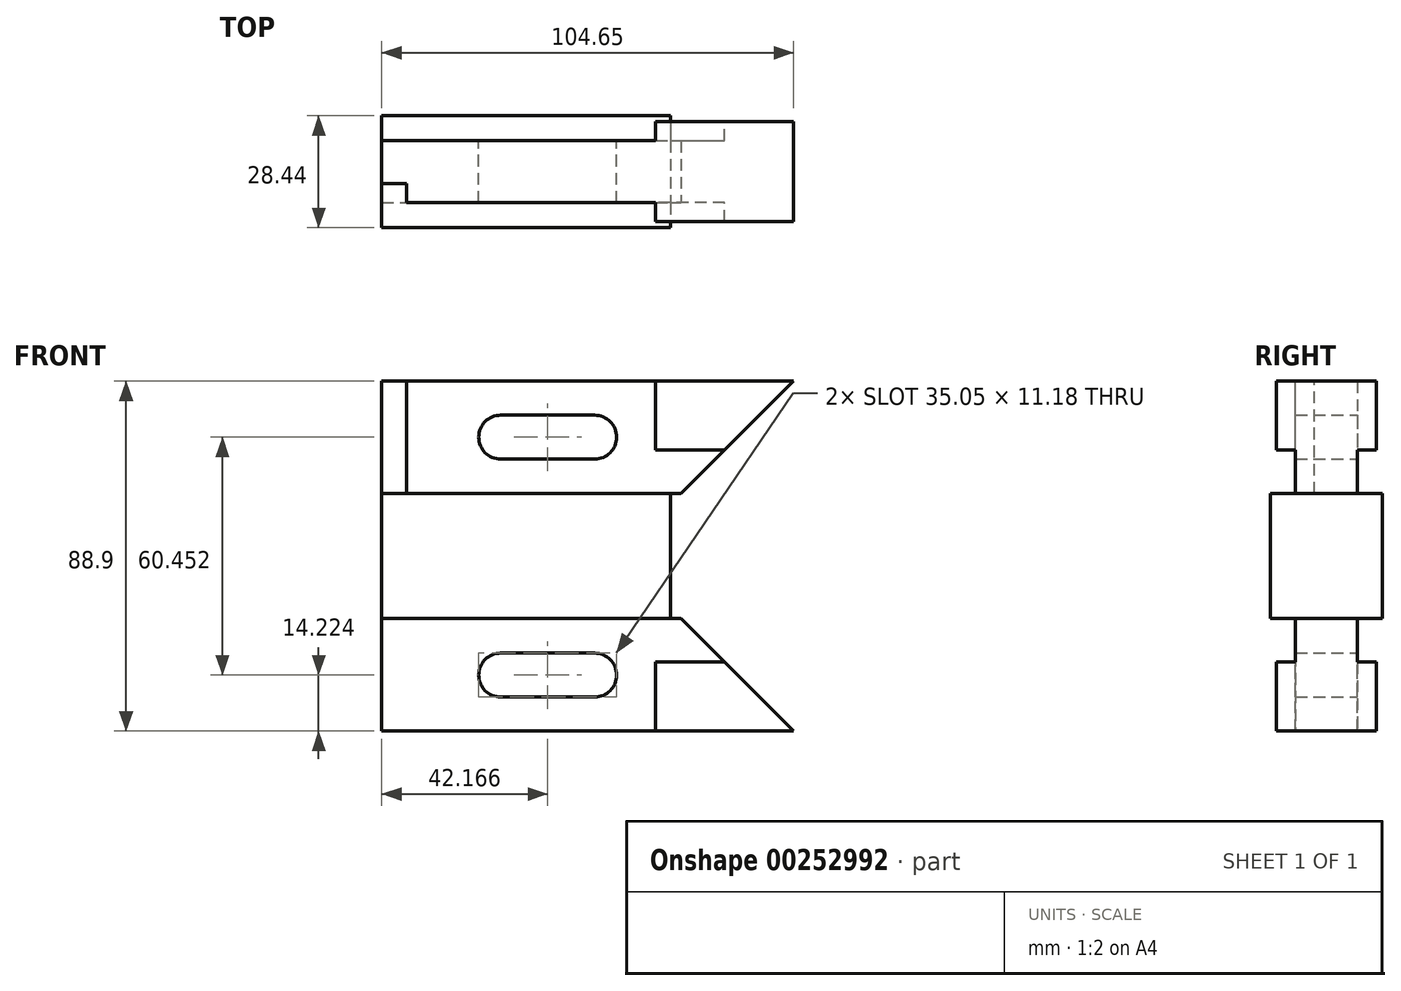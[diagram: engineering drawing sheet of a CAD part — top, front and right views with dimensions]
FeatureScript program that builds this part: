
annotation { "Feature Type Name" : "Feature", "Feature Type Description" : "" }
export const myFeature = defineFeature(function(context is Context, id is Id, definition is map)
    precondition{}
    {
        {
            var Q0;
            Q0=qCreatedBy(makeId("Right.planeOp"),FACE);
            var sketch = newSketch(context, id + "F0", { "sketchPlane" : qUnion([Q0])});
            skLineSegment(sketch, "E0", {"start": v(-14.22, 0) * mm, "end": v(14.22, 0) * mm, "construction": true});
            skLineSegment(sketch, "E1", {"start": v(-14.22, 0) * mm, "end": v(-14.22, 15.88) * mm});
            skLineSegment(sketch, "E2", {"start": v(-7.87, 15.88) * mm, "end": v(-7.87, 44.45) * mm});
            skLineSegment(sketch, "E3", {"start": v(7.87, 15.88) * mm, "end": v(14.22, 15.88) * mm});
            skLineSegment(sketch, "E4", {"start": v(14.22, 0) * mm, "end": v(14.22, 15.88) * mm});
            skLineSegment(sketch, "E5", {"start": v(-7.87, 44.45) * mm, "end": v(7.87, 44.45) * mm});
            skLineSegment(sketch, "E6", {"start": v(7.87, 44.45) * mm, "end": v(7.87, 15.88) * mm});
            skLineSegment(sketch, "E7", {"start": v(-14.22, 15.88) * mm, "end": v(-7.87, 15.88) * mm});
            skLineSegment(sketch, "E8.MirrorCS", {"start": v(14.22, 0) * mm, "end": v(14.22, -15.88) * mm});
            skLineSegment(sketch, "E9.MirrorCS", {"start": v(-14.22, 0) * mm, "end": v(-14.22, -15.88) * mm});
            skLineSegment(sketch, "E10.MirrorCS", {"start": v(-14.22, -15.88) * mm, "end": v(-7.87, -15.88) * mm});
            skLineSegment(sketch, "E11.MirrorCS", {"start": v(7.87, -15.88) * mm, "end": v(14.22, -15.88) * mm});
            skLineSegment(sketch, "E12.MirrorCS", {"start": v(7.87, -44.45) * mm, "end": v(7.87, -15.88) * mm});
            skLineSegment(sketch, "E13.MirrorCS", {"start": v(-7.87, -15.88) * mm, "end": v(-7.87, -44.45) * mm});
            skLineSegment(sketch, "E14.MirrorCS", {"start": v(-7.87, -44.45) * mm, "end": v(7.87, -44.45) * mm});
            skSolve(sketch);
        }
        {
            var Q0;
            Q0=qSketchRegion(id+"F0",true);
            extrude(context, id + "F1", {"entities" : qUnion([Q0]), "oppositeDirection" : true, "depth" : 104.65 * mm});
        }
        {
            var Q0;
            Q0=makeQuery(id+"F1.opExtrude","SWEPT_FACE",FACE,{"disambiguationData":[OSD([sQuery(id+"F0.wireOp",EDGE,"E5")])]});
            var sketch = newSketch(context, id + "F2", { "sketchPlane" : qUnion([Q0])});
            skLineSegment(sketch, "E15.bottom", {"start": v(-104.65, -7.87) * mm, "end": v(-98.3, -7.87) * mm});
            skLineSegment(sketch, "E15.top", {"start": v(-104.65, -3.05) * mm, "end": v(-98.3, -3.05) * mm});
            skLineSegment(sketch, "E15.left", {"start": v(-104.65, -7.87) * mm, "end": v(-104.65, -3.05) * mm});
            skLineSegment(sketch, "E16", {"start": v(-98.3, -3.05) * mm, "end": v(-98.3, -7.87) * mm});
            skSolve(sketch);
        }
        {
            var Q0;
            Q0=qSketchRegion(id+"F2",true);
            var Q1;
            Q1=makeQuery(id+"F1.opExtrude","SWEPT_FACE",FACE,{"disambiguationData":[OSD([sQuery(id+"F0.wireOp",EDGE,"E7")])]});
            extrude(context, id + "F3", {"entities" : qUnion([Q0]), "operationType" : NewBodyOperationType.REMOVE, "endBound" : BoundingType.UP_TO_SURFACE, "oppositeDirection" : true, "endBoundEntityFace" : qUnion([Q1]), "depth" : 25.4 * mm});
        }
        {
            var Q0;
            Q0=qCreatedBy(makeId("Front.planeOp"),FACE);
            var sketch = newSketch(context, id + "F4", { "sketchPlane" : qUnion([Q0])});
            skLineSegment(sketch, "E17", {"start": v(0, 0) * mm, "end": v(-107.27, 0) * mm, "construction": true});
            skArc(sketch, "E18", {"start": v(-74.42, -24.64) * mm, "mid": v(-80.01, -30.23) * mm, "end": v(-74.42, -35.81) * mm});
            skArc(sketch, "E19", {"start": v(-50.55, -35.81) * mm, "mid": v(-44.96, -30.23) * mm, "end": v(-50.55, -24.64) * mm});
            skLineSegment(sketch, "E20", {"start": v(-74.42, -24.64) * mm, "end": v(-50.55, -24.64) * mm});
            skLineSegment(sketch, "E21", {"start": v(-74.42, -35.81) * mm, "end": v(-50.55, -35.81) * mm});
            skLineSegment(sketch, "E22.MirrorCS", {"start": v(-74.42, 24.64) * mm, "end": v(-50.55, 24.64) * mm});
            skArc(sketch, "E23.MirrorCS", {"start": v(-50.55, 35.81) * mm, "mid": v(-44.96, 30.23) * mm, "end": v(-50.55, 24.64) * mm});
            skLineSegment(sketch, "E24.MirrorCS", {"start": v(-74.42, 35.81) * mm, "end": v(-50.55, 35.81) * mm});
            skArc(sketch, "E25.MirrorCS", {"start": v(-74.42, 24.64) * mm, "mid": v(-80.01, 30.23) * mm, "end": v(-74.42, 35.81) * mm});
            skSolve(sketch);
        }
        {
            var Q0;
            Q0=qSketchRegion(id+"F4",true);
            extrude(context, id + "F5", {"entities" : qUnion([Q0]), "operationType" : NewBodyOperationType.REMOVE, "endBound" : BoundingType.SYMMETRIC, "depth" : 137.16 * mm});
        }
        {
            var Q0;
            Q0=qCreatedBy(makeId("Front.planeOp"),FACE);
            var sketch = newSketch(context, id + "F6", { "sketchPlane" : qUnion([Q0])});
            skLineSegment(sketch, "E26", {"start": v(0, 0) * mm, "end": v(-121.21, 0) * mm, "construction": true});
            skPoint(sketch, "E27.0", {"position": v(-101.47, 44.45) * mm});
            skLineSegment(sketch, "E28.0", {"start": v(-104.65, 44.45) * mm, "end": v(-98.3, 44.45) * mm});
            skLineSegment(sketch, "E29.0", {"start": v(-104.65, 15.87) * mm, "end": v(-104.65, 44.45) * mm});
            skLineSegment(sketch, "E30.0", {"start": v(-104.65, -15.88) * mm, "end": v(-104.65, 15.88) * mm});
            skLineSegment(sketch, "E31", {"start": v(-104.65, 44.45) * mm, "end": v(-35.05, 44.45) * mm});
            skLineSegment(sketch, "E32", {"start": v(-35.05, 44.45) * mm, "end": v(-35.05, 26.92) * mm});
            skLineSegment(sketch, "E33", {"start": v(-35.05, 44.45) * mm, "end": v(0, 44.45) * mm});
            skLineSegment(sketch, "E34", {"start": v(-35.05, 26.92) * mm, "end": v(-17.53, 26.92) * mm});
            skLineSegment(sketch, "E35", {"start": v(-17.53, 26.92) * mm, "end": v(0, 44.45) * mm});
            skLineSegment(sketch, "E36.MirrorCS", {"start": v(-17.53, -26.92) * mm, "end": v(0, -44.45) * mm});
            skLineSegment(sketch, "E37.MirrorCS", {"start": v(-35.05, -26.92) * mm, "end": v(-17.53, -26.92) * mm});
            skLineSegment(sketch, "E38.MirrorCS", {"start": v(-35.05, -44.45) * mm, "end": v(-35.05, -26.92) * mm});
            skLineSegment(sketch, "E39.MirrorCS", {"start": v(-35.05, -44.45) * mm, "end": v(0, -44.45) * mm});
            skSolve(sketch);
        }
        {
            var Q0;
            Q0=qSketchRegion(id+"F6",true);
            extrude(context, id + "F7", {"entities" : qUnion([Q0]), "endBound" : BoundingType.SYMMETRIC, "depth" : 25.4 * mm});
        }
        {
            var Q0;
            Q0=makeQuery(id+"F7.opExtrude","SWEPT_BODY",BODY,{"disambiguationData":[OSD([sQuery(id+"F6.wireOp",EDGE,"E36.MirrorCS"),sQuery(id+"F6.wireOp",EDGE,"E37.MirrorCS"),sQuery(id+"F6.wireOp",EDGE,"E38.MirrorCS"),sQuery(id+"F6.wireOp",EDGE,"E39.MirrorCS")])]});
            var Q1;
            Q1=makeQuery(id+"F7.opExtrude","SWEPT_BODY",BODY,{"disambiguationData":[OSD([sQuery(id+"F6.wireOp",EDGE,"E32"),sQuery(id+"F6.wireOp",EDGE,"E33"),sQuery(id+"F6.wireOp",EDGE,"E34"),sQuery(id+"F6.wireOp",EDGE,"E35")])]});
            var Q2;
            Q2=makeQuery(id+"F1.opExtrude","SWEPT_BODY",BODY,{"disambiguationData":[OSD([sQuery(id+"F0.wireOp",EDGE,"E1"),sQuery(id+"F0.wireOp",EDGE,"E2"),sQuery(id+"F0.wireOp",EDGE,"E3"),sQuery(id+"F0.wireOp",EDGE,"E4"),sQuery(id+"F0.wireOp",EDGE,"E5"),sQuery(id+"F0.wireOp",EDGE,"E6"),sQuery(id+"F0.wireOp",EDGE,"E7"),sQuery(id+"F0.wireOp",EDGE,"E8.MirrorCS"),sQuery(id+"F0.wireOp",EDGE,"E9.MirrorCS"),sQuery(id+"F0.wireOp",EDGE,"E10.MirrorCS"),sQuery(id+"F0.wireOp",EDGE,"E11.MirrorCS"),sQuery(id+"F0.wireOp",EDGE,"E12.MirrorCS"),sQuery(id+"F0.wireOp",EDGE,"E13.MirrorCS"),sQuery(id+"F0.wireOp",EDGE,"E14.MirrorCS")])]});
            booleanBodies(context, id + "F8", {"operationType" : BooleanOperationType.UNION, "tools" : qUnion([Q0, Q1, Q2])});
        }
        {
            var Q0;
            Q0=qCreatedBy(makeId("Front.planeOp"),FACE);
            var sketch = newSketch(context, id + "F9", { "sketchPlane" : qUnion([Q0])});
            skLineSegment(sketch, "E40.0", {"start": v(-104.65, 15.88) * mm, "end": v(0, 15.88) * mm});
            skLineSegment(sketch, "E41.0.0", {"start": v(0, -15.88) * mm, "end": v(0, 15.88) * mm});
            skLineSegment(sketch, "E41.0.2", {"start": v(-104.65, 15.88) * mm, "end": v(-104.65, -15.88) * mm});
            skLineSegment(sketch, "E41.0.3", {"start": v(-104.65, -15.88) * mm, "end": v(0, -15.88) * mm});
            skLineSegment(sketch, "E42.0.0", {"start": v(-104.65, -44.45) * mm, "end": v(-35.05, -44.45) * mm});
            skLineSegment(sketch, "E42.0.1", {"start": v(-35.05, -44.45) * mm, "end": v(-35.05, -26.92) * mm});
            skLineSegment(sketch, "E42.0.2", {"start": v(-35.05, -26.92) * mm, "end": v(-17.53, -26.92) * mm});
            skLineSegment(sketch, "E42.0.3", {"start": v(-17.53, -26.92) * mm, "end": v(0, -44.45) * mm});
            skLineSegment(sketch, "E42.0.4", {"start": v(0, -44.45) * mm, "end": v(0, -15.88) * mm});
            skLineSegment(sketch, "E42.0.5", {"start": v(0, -15.88) * mm, "end": v(-104.65, -15.88) * mm});
            skLineSegment(sketch, "E42.0.6", {"start": v(-104.65, -15.88) * mm, "end": v(-104.65, -44.45) * mm});
            skLineSegment(sketch, "E43.0.0", {"start": v(-35.05, -26.92) * mm, "end": v(-35.05, -44.45) * mm});
            skLineSegment(sketch, "E43.0.1", {"start": v(-35.05, -44.45) * mm, "end": v(0, -44.45) * mm});
            skLineSegment(sketch, "E43.0.2", {"start": v(0, -44.45) * mm, "end": v(-17.53, -26.92) * mm});
            skLineSegment(sketch, "E43.0.3", {"start": v(-17.53, -26.92) * mm, "end": v(-35.05, -26.92) * mm});
            skLineSegment(sketch, "E44", {"start": v(-28.58, -15.88) * mm, "end": v(0, -15.88) * mm});
            skSolve(sketch);
        }
        {
            var Q0;
            Q0=qCreatedBy(makeId("Front.planeOp"),FACE);
            var sketch = newSketch(context, id + "F10", { "sketchPlane" : qUnion([Q0])});
            skLineSegment(sketch, "E45.0", {"start": v(-17.53, 26.92) * mm, "end": v(0, 44.45) * mm});
            skLineSegment(sketch, "E46.0", {"start": v(-17.53, -26.92) * mm, "end": v(0, -44.45) * mm});
            skLineSegment(sketch, "E47.0", {"start": v(0, -15.88) * mm, "end": v(-104.65, -15.88) * mm});
            skLineSegment(sketch, "E48.0", {"start": v(-104.65, 15.88) * mm, "end": v(0, 15.88) * mm});
            skLineSegment(sketch, "E49", {"start": v(0, 44.45) * mm, "end": v(-28.58, 15.88) * mm});
            skLineSegment(sketch, "E50", {"start": v(0, 15.88) * mm, "end": v(0, 44.45) * mm});
            skLineSegment(sketch, "E51", {"start": v(0, 15.88) * mm, "end": v(-28.58, 15.88) * mm});
            skLineSegment(sketch, "E52", {"start": v(0, -44.45) * mm, "end": v(-28.58, -15.87) * mm});
            skLineSegment(sketch, "E53", {"start": v(0, -44.45) * mm, "end": v(0, -15.88) * mm});
            skSolve(sketch);
        }
        {
            var Q0;
            Q0=qSketchRegion(id+"F10",true);
            extrude(context, id + "F11", {"entities" : qUnion([Q0]), "operationType" : NewBodyOperationType.REMOVE, "endBound" : BoundingType.SYMMETRIC, "oppositeDirection" : true, "depth" : 78.23 * mm});
        }
        {
            var Q0;
            Q0=qCreatedBy(makeId("Front.planeOp"),FACE);
            var sketch = newSketch(context, id + "F12", { "sketchPlane" : qUnion([Q0])});
            skLineSegment(sketch, "E54.0", {"start": v(0, -15.88) * mm, "end": v(0, 15.88) * mm});
            skLineSegment(sketch, "E55", {"start": v(0, 15.88) * mm, "end": v(0, -15.88) * mm});
            skLineSegment(sketch, "E56", {"start": v(0, 15.88) * mm, "end": v(-31.24, 15.88) * mm});
            skLineSegment(sketch, "E57", {"start": v(0, -15.88) * mm, "end": v(-31.24, -15.88) * mm});
            skLineSegment(sketch, "E58", {"start": v(-31.24, 15.88) * mm, "end": v(-31.24, -15.88) * mm});
            skSolve(sketch);
        }
        {
            var Q0;
            Q0=qSketchRegion(id+"F12",true);
            extrude(context, id + "F13", {"entities" : qUnion([Q0]), "operationType" : NewBodyOperationType.REMOVE, "endBound" : BoundingType.SYMMETRIC, "oppositeDirection" : true, "depth" : 134.62 * mm});
        }
    });
